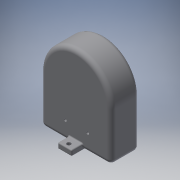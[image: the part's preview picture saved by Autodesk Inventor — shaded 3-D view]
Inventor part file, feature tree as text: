
AUTODESK INVENTOR PART (.ipt)
format: ipt  version: 2018 (Build 220112000, 112)  size: 347,648 bytes
history: native  units: in
note: dims shown in document units (in); Inventor stores cm internally (conversion verified against a paired STEP export)
features: extrude x8, fillet x8, sketch x6, reference x4, projected_geometry x2, other x2, plane x1
ambient origin geometry x8: Origin, YZ Plane, XZ Plane, XY Plane, X Axis, Y Axis, Z Axis, Center Point
bodies: Solid1 (feature_tree)
feature tree (31):
  extrude  "Extrusion1"  Depth=1.0in TaperAngle=0.0deg
  extrude  "Extrusion4"  Depth=0.4in TaperAngle=0.0deg
  extrude  "Extrusion5"  Depth=0.1772in
  extrude  "Extrusion6"  Depth=0.25in
  extrude  "Extrusion8"  Depth=0.197in
  plane  "Work Plane1"
  extrude  "Extrusion10"  Depth=1.0in
  fillet  "Fillet1"  Radius=0.25in
  fillet  "Fillet2"  Radius=0.5in
  fillet  "Fillet3"  Radius=0.197in
  fillet  "Fillet4"  Radius=0.15in
  fillet  "Fillet5"  Radius=0.1378in
  fillet  "Fillet6"  Radius=0.4in
  fillet  "Fillet7"  [1 undecoded]
  extrude  "Extrusion11"  Depth=1.0in
  fillet  "Fillet10"  Radius=0.0787in
  extrude  "Extrusion12"  Depth=1.0in TaperAngle=0.0deg
  sketch  "Sketch1"  dims[d0=2.5in d1=1.0in d2=0.0in]
  reference  "Reference1"
  sketch  "Sketch4"  dims[d9=0.197in d10=0.4in d11=0.0in]
  sketch  "Sketch7"  dims[d12=0.15in d13=0.1772in]
  sketch  "Sketch9"  dims[d14=0.4in d15=0.0in d16=0.25in]
  reference  "Reference3"
  reference  "Reference4"
  sketch  "Sketch10"  dims[d17=0.5in d18=0.197in]
  reference  "Reference5"
  sketch  "Sketch11"  dims[d19=0.4in d20=0.0in d25=0.5in d26=0.25in d27=0.5in d28=0.197in d29=0.15in d30=0.1378in d31=0.4in d32=0.0in d33=-1.25in d40=0.0787in d41=0.0787in d42=1.0in d43=0.0in d44=0.098in d45=0.1575in d46=0.1575in d47=0.0394in d48=0.0394in d49=0.0394in d50=0.0394in d51=0.0394in d55=0.1181in d56=0.75in d57=0.0in d58=0.0197in d59=0.5in d60=0.1181in d61=1.0in d62=0.0in]
  projected_geometry  "Projected Loop1"
  projected_geometry  "Projected Loop2"
  other  "Glyptodon.iam"
  other  "SyringeTailLeverAttachment:1"
note: 1 required parameter value undecoded (feature->parameter linkage not recoverable at this tier; creation-order binding heuristic only, values carry confidence <= 0.55)
